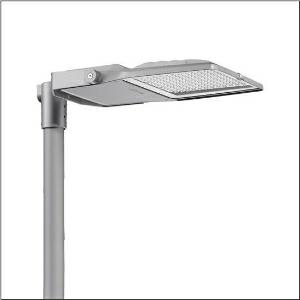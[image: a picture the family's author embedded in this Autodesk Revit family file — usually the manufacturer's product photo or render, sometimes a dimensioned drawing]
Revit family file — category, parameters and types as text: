
# Revit family: floodlight_fl_21_iq_midi___pl33t_5xa7781e6f3a_cd97
name_source: partatom
category: Lighting Fixtures
units: mm (PartAtom-declared; Revit-internal decimal feet)

## family parameters
Cut with Voids When Loaded = No
Host = Face
Light Source = No
Part Type = Normal
Room Calculation Point = No
Round Connector Dimension = Use Diameter
Shared = No

## types (1)
- --- (1 x LED, 21270 lm, 208.1 W, 5700K)
    Apparent Load = 208 VA
    CIE Flux Codes = 26 75 99 100 100
    Color Rendering = 90
    Color Temperature = 5700K
    Default Elevation = 1800 mm
    Description = Floodlight FL 21 iQ midi, floodlight, primary light control with lens, of PMMA, primary optical cover: protective disc, of toughened safety glass, transparent, light distribution: PL33T, light emission: direct distribution, installation type: surface-mounted, lamps: LED, High Power LED, rated values: 21.270lm | 208,1W | 102,2lm/W (begin service life); end service life: 21.270lm | 227,1W; at 50% lumin. flux: 10.635lm | 90W | 118,2lm/W, colour temperature: 5700K, colour rendering: CRI > 90, light colour: 957, light setting 1 begin service life: 100% | 21.270lm | 208,1W | 102,2lm/W | 5.700K, light setting 1 end service life: 227,1W, further light settings possible, control: optimised constant luminous flux control (CLO 2.0), Desk-Remote (wireless, voltage-free reading and setting of iQ features in the workshop via application-optimized NFC function/RFID function), Light-Fading, Smart-Wire, Night-Set, Lumen-Switch, Temp-Guard, Auto-Match, pre-setting: linear dimming characteristic, with terminal, 6-pole, mains connection: 220..240V, AC, 50/60Hz, luminaire housing, of diecast aluminium, powder-coated, SITECO metallic grey (DB 702S), corrosivity category C5 mid according to DIN EN ISO 12944suitable for swimming poolschlorine-resistant, sealing non-destructively replaceable, please order mast flange separately, mast bracket, of steel, galvanised, powder-coated, SITECO metallic grey (DB 702S), protection rating (complete): IP66, insulation class (complete): insulation class II (safety insulation), certification: CE, ENEC, VDE, protection symbol: D, impact resistance: IK08, permissible operating ambient temperature: -40..+40°C, permissible operating ambient temperature for outdoor applications: -40..+50°C, standard: DIN EN 12944, LABS conformity tested according to VDMA 24364:2018-05, packaging unit: 1 piece

Light Distribution: PL33T
    Height = 76 mm
    Lamp = 1 x LED
    Lamp Light Flux = 21270 lm
    Lamp Power = 208.1 W
    Lamp count = 1
    Length = 657 mm
    Luminous efficacy = 102 lm/W
    Manufacturer = Siteco
    ModVariant = No
    Model = 5XA7781E6F3A
    Number of Poles = 1
    OnlyDefault = Yes
    Power Factor = 1
    Product Name = Floodlight FL 21 iQ midi | PL33T
    Product group = floodlight | pylon annexe
    ProductGroupID = 6201
    Protection Class = Protection class II
    Protection Degree = IP 66
    RLX_Detail_Level = 1
    RLX_Emergency_Light_Flux = 0 lm
    RLX_Emergency_Type = 0
    RLX_Emergency_Type_DB = No
    RlxData = <blob elided: 153937 chars, md5=aca29770>
    Socket = socket
    Standby Power = 0 W
    System Light Flux = 21270 lm
    System Power = 208 W
    Type Comments = factory setting: luminous flux: 100 % | dim-lin: 254 | 710 mA
    Type Image = l_1007123.jpg
    URL = http://relux.com
    VarID = @adj_103585
    Voltage = 0 V
    Weight = 0.00 kg
    Width = 442 mm

## geometry (parser evidence)
native form markers: Blend x4, Sweep x14
no freeform markers — native parametric forms only
